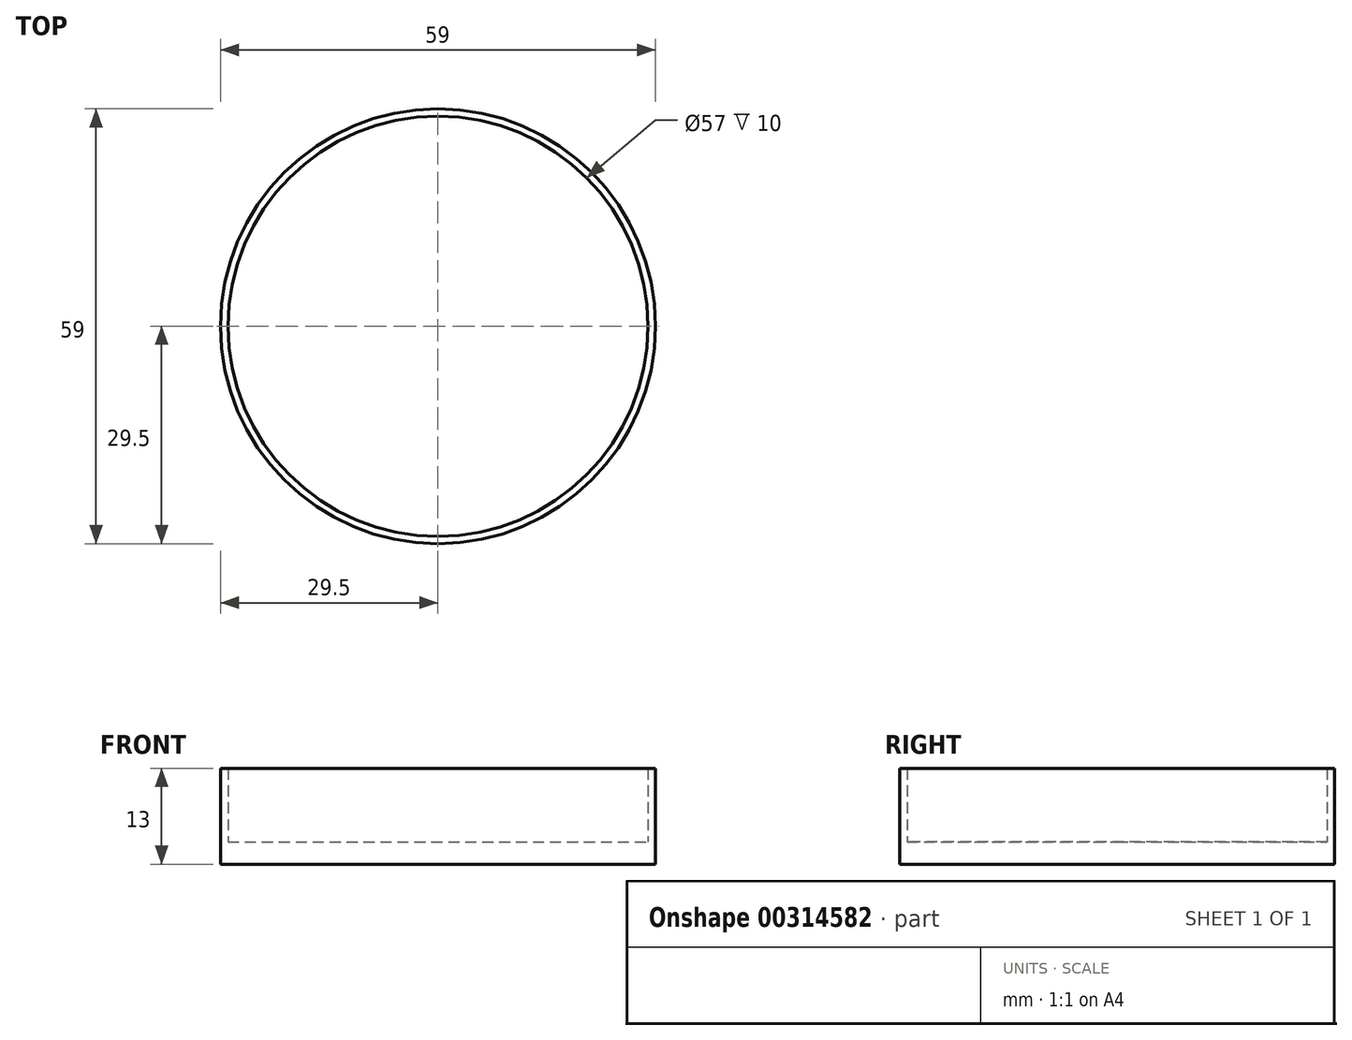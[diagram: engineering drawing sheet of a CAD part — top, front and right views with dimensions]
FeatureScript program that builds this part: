
annotation { "Feature Type Name" : "Feature", "Feature Type Description" : "" }
export const myFeature = defineFeature(function(context is Context, id is Id, definition is map)
    precondition{}
    {
        {
            var Q0;
            Q0=qCreatedBy(makeId("Top.planeOp"),FACE);
            var sketch = newSketch(context, id + "F0", { "sketchPlane" : qUnion([Q0])});
            skCircle(sketch, "E0", {"center": v(0, 0) * mm, "radius": 29.5 * mm});
            skSolve(sketch);
        }
        {
            var Q0;
            Q0=qCreatedBy(makeId("Top.planeOp"),FACE);
            var sketch = newSketch(context, id + "F1", { "sketchPlane" : qUnion([Q0])});
            skCircle(sketch, "E1", {"center": v(0, 0) * mm, "radius": 29 * mm});
            skSolve(sketch);
        }
        {
            var Q0;
            Q0 = qSketchRegion(id + "F0", true);
            extrude(context, id + "F2", {"entities" : qUnion([Q0]), "depth" : 10 * mm});
        }
        {
            var Q0;
            Q0=sQuery(id+"F1.wireOp",VERTEX,"E1.center");
            var Q1;
            Q1=makeQuery(id+"F2.opExtrude","SWEPT_BODY",BODY,{"disambiguationData":[OSD([sQuery(id+"F0.wireOp",EDGE,"E0")])]});
            hole(context, id + "F3", {"style" : HoleStyle.SIMPLE, "endStyle" : HoleEndStyle.THROUGH, "oppositeDirection" : true, "holeDiameter" : 57 * mm, "tappedDepth" : 12.7 * mm, "tapClearance" : 3, "locations" : qUnion([Q0]), "scope" : qUnion([Q1])});
        }
        {
            var Q0;
            Q0=qCreatedBy(makeId("Top.planeOp"),FACE);
            cPlane(context, id + "F4", {"entities" : qUnion([Q0]), "cplaneType" : CPlaneType.OFFSET, "offset" : 3 * mm, "oppositeDirection" : true, "width" : 152.4 * mm, "height" : 152.4 * mm});
        }
        {
            var Q0;
            Q0=qCreatedBy(id+"F4.planeOp",FACE);
            var sketch = newSketch(context, id + "F5", { "sketchPlane" : qUnion([Q0])});
            skCircle(sketch, "E2", {"center": v(0, 0) * mm, "radius": 29.5 * mm});
            skSolve(sketch);
        }
        {
            var Q0;
            Q0 = qSketchRegion(id + "F5", true);
            extrude(context, id + "F6", {"entities" : qUnion([Q0]), "operationType" : NewBodyOperationType.ADD, "depth" : 3 * mm});
        }
    });
